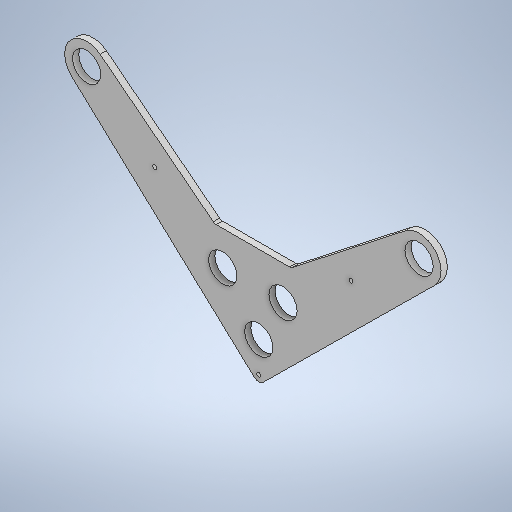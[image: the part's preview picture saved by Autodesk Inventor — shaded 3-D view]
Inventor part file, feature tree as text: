
AUTODESK INVENTOR PART (.ipt)
format: ipt  version: 2025.1 (Build 291241020, 241B)  size: 301,568 bytes
history: native  units: in
note: dims shown in document units (in); Inventor stores cm internally (conversion verified against a paired STEP export)
features: sketch x1, extrude x1
ambient origin geometry x8: Origin, YZ Plane, XZ Plane, XY Plane, X Axis, Y Axis, Z Axis, Center Point
bodies: Solid1 (feature_tree)
feature tree (2):
  sketch  "Sketch1"  dims[d0=4.0in d1=4.0in d2=0.159in d3=0.5in d4=3.4395in d5=0.5in d6=0.063in d7=0.159in d8=0.5in d9=0.159in d10=3.4395in d11=0.063in d12=0.188in d13=1.75in d14=1.75in d15=1.125in d16=0.7146in d17=6.879in d18=1.654in d19=1.504in d20=1.125in d21=0.063in d22=0.1in d23=2.4in d24=0.1in d25=1.6in d27=0.0in d28=0.25in]
  extrude  "Extrusion1"  [1 undecoded]
note: 1 required parameter value undecoded (feature->parameter linkage not recoverable at this tier; creation-order binding heuristic only, values carry confidence <= 0.55)
